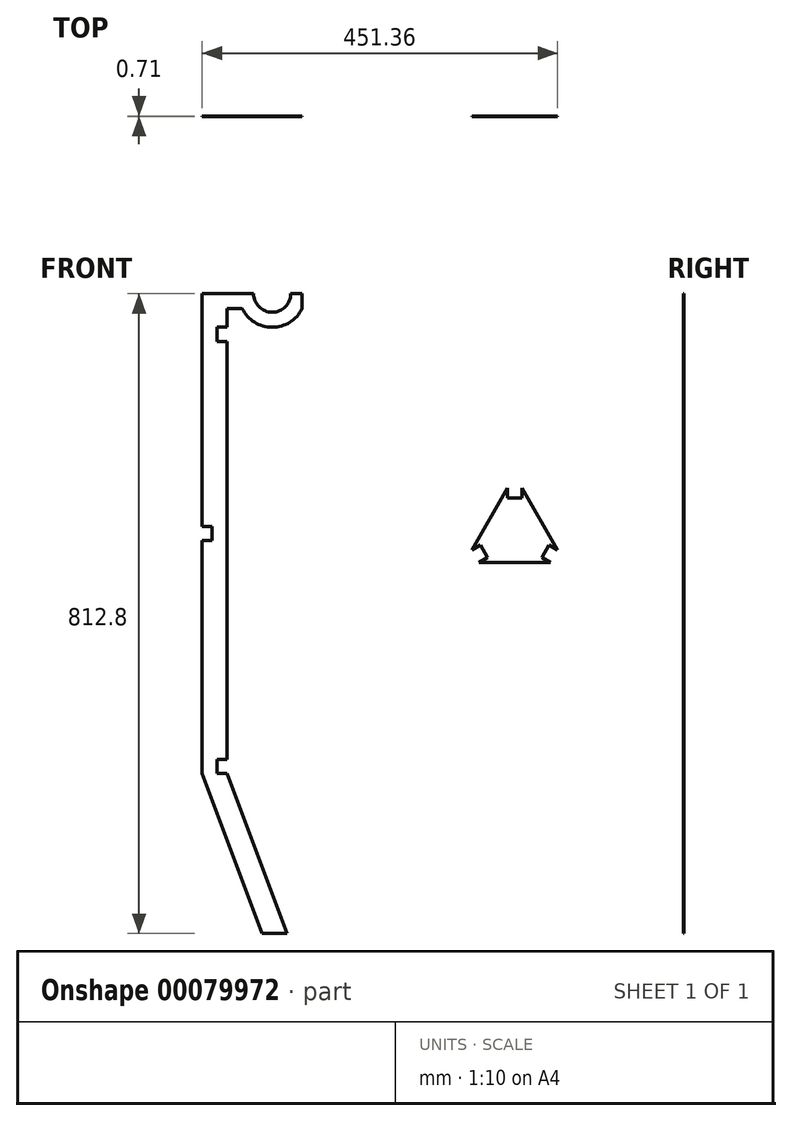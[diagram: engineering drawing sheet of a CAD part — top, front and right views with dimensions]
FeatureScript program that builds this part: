
annotation { "Feature Type Name" : "Feature", "Feature Type Description" : "" }
export const myFeature = defineFeature(function(context is Context, id is Id, definition is map)
    precondition{}
    {
        {
            assignVariable(context, id + "F0", {"name" : "thickness", "anyValue" : .71});
        }
        {
            var Q0;
            Q0=qCreatedBy(makeId("Front.planeOp"),FACE);
            var sketch = newSketch(context, id + "F1", { "sketchPlane" : qUnion([Q0])});
            skLineSegment(sketch, "E0.bottom", {"start": v(15.87, 304.8) * mm, "end": v(-15.88, 304.8) * mm});
            skLineSegment(sketch, "E0.top", {"start": v(15.87, -304.8) * mm, "end": v(-15.88, -304.8) * mm});
            skLineSegment(sketch, "E0.left", {"start": v(15.87, 304.8) * mm, "end": v(15.87, -304.8) * mm});
            skLineSegment(sketch, "E0.right", {"start": v(-15.88, 304.8) * mm, "end": v(-15.88, -304.8) * mm});
            skPoint(sketch, "E0.middle", {"position": v(0, 0) * mm});
            skLineSegment(sketch, "E1", {"start": v(-15.88, -304.8) * mm, "end": v(60.32, -508) * mm});
            skLineSegment(sketch, "E2", {"start": v(15.87, -304.8) * mm, "end": v(92.07, -508) * mm});
            skLineSegment(sketch, "E3", {"start": v(60.32, -508) * mm, "end": v(92.07, -508) * mm});
            skLineSegment(sketch, "E4.bottom", {"start": v(15.87, -304.8) * mm, "end": v(3.17, -304.8) * mm});
            skLineSegment(sketch, "E4.top", {"start": v(15.87, -286.77) * mm, "end": v(3.17, -286.77) * mm});
            skLineSegment(sketch, "E4.left", {"start": v(15.87, -304.8) * mm, "end": v(15.87, -286.77) * mm});
            skLineSegment(sketch, "E4.right", {"start": v(3.17, -304.8) * mm, "end": v(3.17, -286.77) * mm});
            skLineSegment(sketch, "E5.bottom", {"start": v(15.87, 304.8) * mm, "end": v(34.92, 304.8) * mm});
            skLineSegment(sketch, "E5.top", {"start": v(15.87, 285.75) * mm, "end": v(34.92, 285.75) * mm});
            skLineSegment(sketch, "E5.left", {"start": v(15.87, 304.8) * mm, "end": v(15.87, 285.75) * mm});
            skLineSegment(sketch, "E5.right", {"start": v(34.92, 304.8) * mm, "end": v(34.92, 285.75) * mm});
            skArc(sketch, "E6", {"start": v(34.92, 285.75) * mm, "mid": v(73.02, 262.2) * mm, "end": v(111.12, 285.75) * mm});
            skArc(sketch, "E7.0", {"start": v(49.48, 304.8) * mm, "mid": v(73.02, 281.25) * mm, "end": v(96.57, 304.8) * mm});
            skLineSegment(sketch, "E8", {"start": v(96.57, 304.8) * mm, "end": v(111.12, 304.8) * mm});
            skLineSegment(sketch, "E9", {"start": v(111.12, 285.75) * mm, "end": v(111.12, 304.8) * mm});
            skLineSegment(sketch, "E10", {"start": v(49.48, 304.8) * mm, "end": v(34.92, 304.8) * mm});
            skPoint(sketch, "E11.firstSnap0", {"position": v(73.02, 262.2) * mm});
            skLineSegment(sketch, "E11.bottom", {"start": v(15.87, 262.2) * mm, "end": v(3.17, 262.2) * mm});
            skLineSegment(sketch, "E11.top", {"start": v(15.87, 244.17) * mm, "end": v(3.17, 244.17) * mm});
            skLineSegment(sketch, "E11.left", {"start": v(15.87, 262.2) * mm, "end": v(15.87, 244.17) * mm});
            skLineSegment(sketch, "E11.right", {"start": v(3.17, 262.2) * mm, "end": v(3.17, 244.17) * mm});
            skLineSegment(sketch, "E12.bottom", {"start": v(-15.88, 0) * mm, "end": v(-3.18, 0) * mm});
            skLineSegment(sketch, "E12.top", {"start": v(-15.88, 9.02) * mm, "end": v(-3.18, 9.02) * mm});
            skLineSegment(sketch, "E12.left", {"start": v(-15.88, 0) * mm, "end": v(-15.88, 9.02) * mm});
            skLineSegment(sketch, "E12.right", {"start": v(-3.18, 0) * mm, "end": v(-3.18, 9.02) * mm});
            skLineSegment(sketch, "E13.MirrorCS", {"start": v(-3.18, 0) * mm, "end": v(-3.18, -9.02) * mm});
            skLineSegment(sketch, "E14.MirrorCS", {"start": v(-15.88, -9.02) * mm, "end": v(-3.18, -9.02) * mm});
            skCircle(sketch, "E15.cCircle", {"center": v(381, 0) * mm, "radius": 36.66 * mm, "construction": true});
            skLineSegment(sketch, "E15.0", {"start": v(381, 73.32) * mm, "end": v(444.5, -36.66) * mm});
            skLineSegment(sketch, "E15.1", {"start": v(444.5, -36.66) * mm, "end": v(317.5, -36.66) * mm});
            skLineSegment(sketch, "E15.2", {"start": v(317.5, -36.66) * mm, "end": v(381, 73.32) * mm});
            skPoint(sketch, "E15.0.midPoint", {"position": v(412.75, 18.33) * mm});
            skLineSegment(sketch, "E16", {"start": v(371.98, 57.7) * mm, "end": v(390.02, 57.7) * mm});
            skLineSegment(sketch, "E17.top", {"start": v(371.98, 45) * mm, "end": v(390.02, 45) * mm});
            skLineSegment(sketch, "E17.left", {"start": v(371.98, 57.7) * mm, "end": v(371.98, 45) * mm});
            skLineSegment(sketch, "E17.right", {"start": v(390.02, 57.7) * mm, "end": v(390.02, 45) * mm});
            skLineSegment(sketch, "E18.1.0", {"start": v(346.53, -30.31) * mm, "end": v(337.52, -14.7) * mm});
            skLineSegment(sketch, "E18.1.1", {"start": v(326.52, -21.04) * mm, "end": v(337.52, -14.7) * mm});
            skLineSegment(sketch, "E18.1.2", {"start": v(335.53, -36.66) * mm, "end": v(346.53, -30.31) * mm});
            skLineSegment(sketch, "E18.2.0", {"start": v(424.48, -14.7) * mm, "end": v(415.47, -30.31) * mm});
            skLineSegment(sketch, "E18.2.1", {"start": v(426.47, -36.66) * mm, "end": v(415.47, -30.31) * mm});
            skLineSegment(sketch, "E18.2.2", {"start": v(435.48, -21.04) * mm, "end": v(424.48, -14.7) * mm});
            skSolve(sketch);
        }
        {
            var Q0;
            {var subQ5=sQuery(id+"F1.wireOp",EDGE,"E0.bottom");Q0=makeQuery(id+"F1.imprint","IMPRINT",FACE,{"disambiguationData":[TD([[makeQuery(id+"F1.imprint","IMPRINT",EDGE,{"derivedFrom":subQ5}),1.0]])]});}
            var Q1;
            Q1=makeQuery(id+"F1.imprint","IMPRINT",FACE,{"disambiguationData":[TD([[makeQuery(id+"F1.imprint","IMPRINT",EDGE,{"derivedFrom":sQuery(id+"F1.wireOp",EDGE,"E5.right")}),1.0]])]});
            var Q2;
            Q2=makeQuery(id+"F1.imprint","IMPRINT",FACE,{"disambiguationData":[TD([[makeQuery(id+"F1.imprint","IMPRINT",EDGE,{"derivedFrom":sQuery(id+"F1.wireOp",EDGE,"E5.bottom")}),-1.0]])]});
            var Q3;
            Q3=makeQuery(id+"F1.imprint","IMPRINT",FACE,{"disambiguationData":[TD([[makeQuery(id+"F1.imprint","IMPRINT",EDGE,{"derivedFrom":sQuery(id+"F1.wireOp",EDGE,"E0.top")}),1.0]])]});
            var Q4;
            Q4=makeQuery(id+"F1.imprint","IMPRINT",FACE,{"disambiguationData":[TD([[makeQuery(id+"F1.imprint","IMPRINT",EDGE,{"derivedFrom":sQuery(id+"F1.wireOp",EDGE,"E17.top")}),-1.0]])]});
            extrude(context, id + "F2", {"entities" : qUnion([Q0, Q1, Q2, Q3, Q4]), "depth" : (getVariable(context, 'thickness')) * mm});
        }
    });
